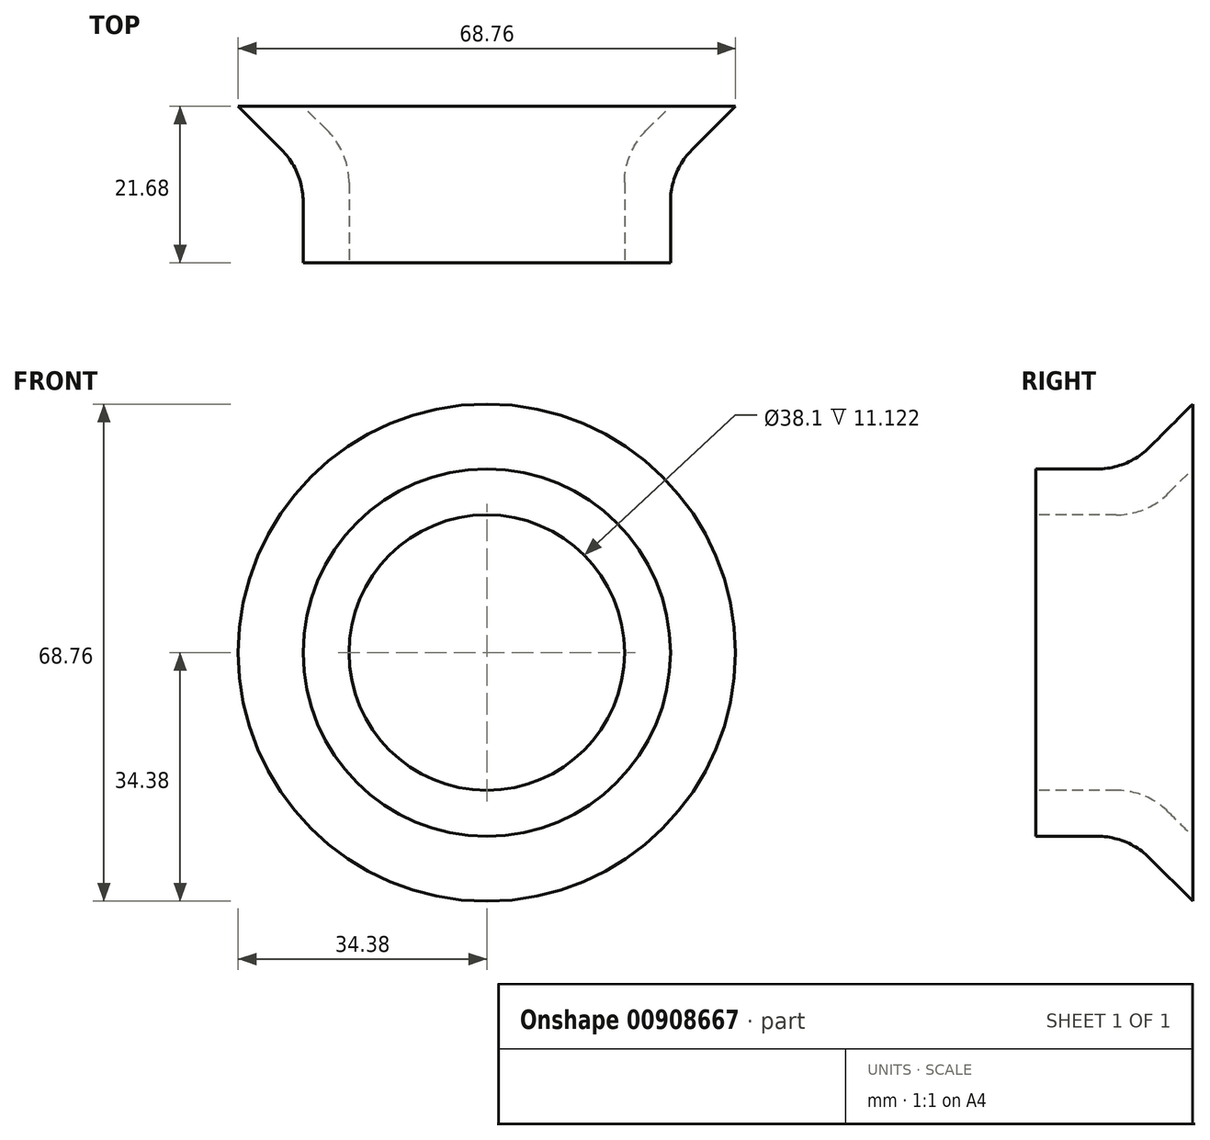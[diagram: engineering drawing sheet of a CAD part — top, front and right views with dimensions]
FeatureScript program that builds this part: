
annotation { "Feature Type Name" : "Feature", "Feature Type Description" : "" }
export const myFeature = defineFeature(function(context is Context, id is Id, definition is map)
    precondition{}
    {
        {
            var Q0;
            Q0=qCreatedBy(makeId("Top.planeOp"),FACE);
            var sketch = newSketch(context, id + "F0", { "sketchPlane" : qUnion([Q0])});
            skLineSegment(sketch, "E0", {"start": v(-25.4, 0) * mm, "end": v(-25.4, 12.7) * mm});
            skLineSegment(sketch, "E1", {"start": v(-25.4, 12.7) * mm, "end": v(-34.38, 21.68) * mm});
            skLineSegment(sketch, "E2.0", {"start": v(-19.05, 15.33) * mm, "end": v(-25.4, 21.68) * mm});
            skLineSegment(sketch, "E2.1", {"start": v(-19.05, 0) * mm, "end": v(-19.05, 15.33) * mm});
            skLineSegment(sketch, "E3", {"start": v(-25.4, 21.68) * mm, "end": v(-34.38, 21.68) * mm});
            skLineSegment(sketch, "E4", {"start": v(-25.4, 0) * mm, "end": v(-19.05, 0) * mm});
            skLineSegment(sketch, "E5", {"start": v(0, 0) * mm, "end": v(0, 44.07) * mm, "construction": true});
            skSolve(sketch);
        }
        {
            var Q0;
            Q0=qSketchRegion(id+"F0",true);
            var Q1;
            Q1=sQuery(id+"F0.wireOp",EDGE,"E5");
            revolve(context, id + "F1", {"surfaceOperationType" : NewSurfaceOperationType.NEW, "entities" : qUnion([Q0]), "axis" : qUnion([Q1]), "revolveType" : RevolveType.FULL});
        }
        {
            var Q0;
            Q0=makeQuery(id+"F1.opRevolve","SWEPT_EDGE",EDGE,{"disambiguationData":[OSD([sQuery(id+"F0.wireOp",EDGE,"E0"),sQuery(id+"F0.wireOp",EDGE,"E1")])]});
            var Q1;
            Q1=makeQuery(id+"F1.opRevolve","SWEPT_EDGE",EDGE,{"disambiguationData":[OSD([sQuery(id+"F0.wireOp",EDGE,"E2.0"),sQuery(id+"F0.wireOp",EDGE,"E2.1")])]});
            fillet(context, id + "F2", {"entities" : qUnion([Q0, Q1]), "radius" : 10.16 * mm, "tangentPropagation" : true, "allowEdgeOverflow" : false});
        }
    });
